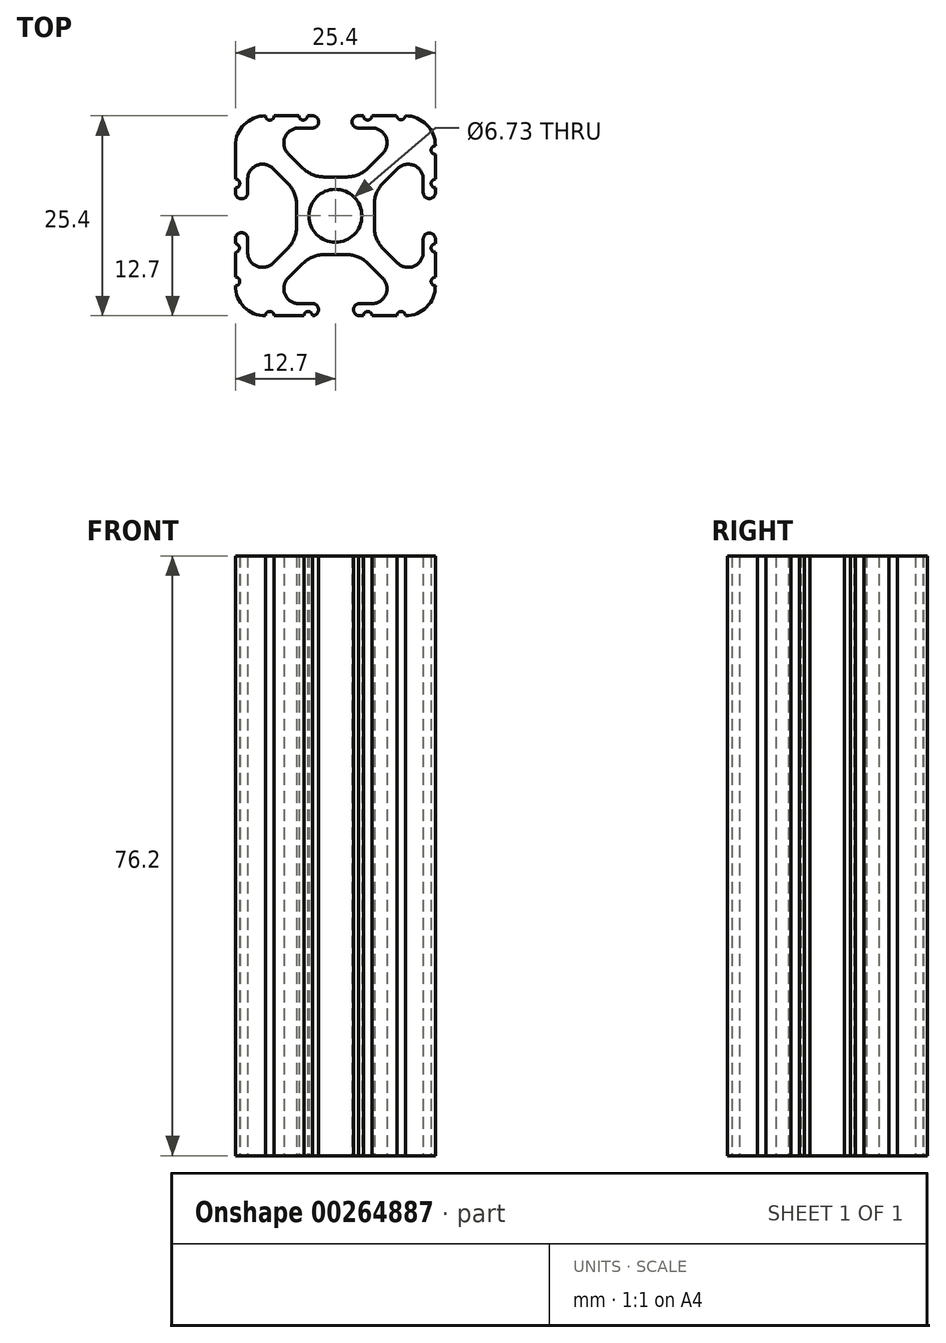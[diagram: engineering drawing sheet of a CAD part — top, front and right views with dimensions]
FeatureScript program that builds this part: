
annotation { "Feature Type Name" : "Feature", "Feature Type Description" : "" }
export const myFeature = defineFeature(function(context is Context, id is Id, definition is map)
    precondition{}
    {
        {
            var Q0;
            Q0=qCreatedBy(makeId("Top.planeOp"),FACE);
            var sketch = newSketch(context, id + "F0", { "sketchPlane" : qUnion([Q0])});
            skCircle(sketch, "E0", {"center": v(-12.7, 12.7) * mm, "radius": 3.36 * mm});
            skLineSegment(sketch, "E1.bottom", {"start": v(-11.24, 17.64) * mm, "end": v(-14.16, 17.64) * mm});
            skLineSegment(sketch, "E1.top", {"start": v(-11.24, 7.76) * mm, "end": v(-14.16, 7.76) * mm});
            skLineSegment(sketch, "E1.left", {"start": v(-7.76, 14.16) * mm, "end": v(-7.76, 11.24) * mm});
            skLineSegment(sketch, "E1.right", {"start": v(-17.64, 14.16) * mm, "end": v(-17.64, 11.24) * mm});
            skPoint(sketch, "E2.visualSharp", {"position": v(-25.4, 25.4) * mm});
            skPoint(sketch, "E3.visualSharp", {"position": v(0, 25.4) * mm});
            skPoint(sketch, "E4.visualSharp", {"position": v(0, 0) * mm});
            skPoint(sketch, "E5.visualSharp", {"position": v(-25.4, 0) * mm});
            skLineSegment(sketch, "E6.0", {"start": v(-18.7, 20.6) * mm, "end": v(-16.85, 18.76) * mm});
            skLineSegment(sketch, "E7.0", {"start": v(-20.6, 18.7) * mm, "end": v(-18.76, 16.85) * mm});
            skPoint(sketch, "E8.orphan", {"position": v(-23.85, 1.55) * mm});
            skPoint(sketch, "E9.orphan", {"position": v(-23.85, 23.85) * mm});
            skPoint(sketch, "E10.orphan", {"position": v(-1.55, 23.85) * mm});
            skPoint(sketch, "E11.orphan", {"position": v(-1.55, 1.55) * mm});
            skLineSegment(sketch, "E12", {"start": v(-8.55, 6.64) * mm, "end": v(-6.7, 4.8) * mm});
            skLineSegment(sketch, "E13.0", {"start": v(-18.7, 4.8) * mm, "end": v(-16.85, 6.64) * mm});
            skLineSegment(sketch, "E14.0", {"start": v(-20.6, 6.7) * mm, "end": v(-18.76, 8.55) * mm});
            skLineSegment(sketch, "E15.0", {"start": v(-8.55, 18.76) * mm, "end": v(-6.7, 20.6) * mm});
            skPoint(sketch, "E16.visualSharp", {"position": v(-23.85, 21.95) * mm});
            skArc(sketch, "E16.filletArc", {"start": v(-20.6, 18.7) * mm, "mid": v(-22.68, 19.1) * mm, "end": v(-23.85, 17.35) * mm});
            skPoint(sketch, "E17.visualSharp", {"position": v(-21.95, 23.85) * mm});
            skArc(sketch, "E17.filletArc", {"start": v(-17.35, 23.85) * mm, "mid": v(-19.1, 22.68) * mm, "end": v(-18.7, 20.6) * mm});
            skPoint(sketch, "E18.visualSharp", {"position": v(-5.34, 23.85) * mm});
            skLineSegment(sketch, "E19", {"start": v(-17.35, 23.85) * mm, "end": v(-15.58, 23.85) * mm});
            skLineSegment(sketch, "E20", {"start": v(-23.85, 17.35) * mm, "end": v(-23.85, 15.62) * mm});
            skLineSegment(sketch, "E21", {"start": v(-8.05, 1.55) * mm, "end": v(-9.78, 1.55) * mm});
            skArc(sketch, "E22.filletArc", {"start": v(-6.7, 20.6) * mm, "mid": v(-6.3, 22.68) * mm, "end": v(-8.05, 23.85) * mm});
            skPoint(sketch, "E23.visualSharp", {"position": v(-1.55, 3.45) * mm});
            skPoint(sketch, "E24.visualSharp", {"position": v(-3.45, 1.55) * mm});
            skArc(sketch, "E24.filletArc", {"start": v(-8.05, 1.55) * mm, "mid": v(-6.3, 2.73) * mm, "end": v(-6.7, 4.8) * mm});
            skArc(sketch, "E25.filletArc", {"start": v(-18.7, 4.8) * mm, "mid": v(-19.1, 2.73) * mm, "end": v(-17.35, 1.55) * mm});
            skArc(sketch, "E26.filletArc", {"start": v(-23.85, 8.05) * mm, "mid": v(-22.68, 6.3) * mm, "end": v(-20.6, 6.7) * mm});
            skLineSegment(sketch, "E27.bottom", {"start": v(-4.9, 0) * mm, "end": v(-8.05, 0) * mm});
            skLineSegment(sketch, "E27.top", {"start": v(-4.92, 25.4) * mm, "end": v(-8.05, 25.4) * mm});
            skLineSegment(sketch, "E27.left", {"start": v(0, 4.9) * mm, "end": v(0, 8.05) * mm});
            skLineSegment(sketch, "E27.right", {"start": v(-25.4, 4.9) * mm, "end": v(-25.4, 8.05) * mm});
            skArc(sketch, "E28.filletArc", {"start": v(-25.4, 3.81) * mm, "mid": v(-24.28, 1.12) * mm, "end": v(-21.59, 0) * mm});
            skArc(sketch, "E29.filletArc", {"start": v(-3.81, 0) * mm, "mid": v(-1.12, 1.12) * mm, "end": v(0, 3.8) * mm});
            skArc(sketch, "E30.filletArc", {"start": v(0, 21.59) * mm, "mid": v(-1.12, 24.28) * mm, "end": v(-3.8, 25.4) * mm});
            skArc(sketch, "E31.filletArc", {"start": v(-21.59, 25.4) * mm, "mid": v(-24.28, 24.28) * mm, "end": v(-25.4, 21.59) * mm});
            skPoint(sketch, "E32.newPointA", {"position": v(-17.64, 7.76) * mm});
            skArc(sketch, "E32.filletArc", {"start": v(-14.16, 7.76) * mm, "mid": v(-15.62, 7.47) * mm, "end": v(-16.85, 6.64) * mm});
            skPoint(sketch, "E33.newPointA", {"position": v(-7.76, 7.76) * mm});
            skArc(sketch, "E33.filletArc", {"start": v(-8.55, 6.64) * mm, "mid": v(-9.78, 7.47) * mm, "end": v(-11.24, 7.76) * mm});
            skArc(sketch, "E34.filletArc", {"start": v(-7.76, 11.24) * mm, "mid": v(-7.47, 9.78) * mm, "end": v(-6.64, 8.55) * mm});
            skArc(sketch, "E35.filletArc", {"start": v(-6.64, 16.85) * mm, "mid": v(-7.47, 15.62) * mm, "end": v(-7.76, 14.16) * mm});
            skPoint(sketch, "E36.newPointB", {"position": v(-7.76, 17.64) * mm});
            skArc(sketch, "E36.filletArc", {"start": v(-11.24, 17.64) * mm, "mid": v(-9.78, 17.93) * mm, "end": v(-8.55, 18.76) * mm});
            skPoint(sketch, "E37.newPointB", {"position": v(-17.64, 17.64) * mm});
            skArc(sketch, "E37.filletArc", {"start": v(-16.85, 18.76) * mm, "mid": v(-15.62, 17.93) * mm, "end": v(-14.16, 17.64) * mm});
            skArc(sketch, "E38.filletArc", {"start": v(-17.64, 14.16) * mm, "mid": v(-17.93, 15.62) * mm, "end": v(-18.76, 16.85) * mm});
            skArc(sketch, "E39.filletArc", {"start": v(-18.76, 8.55) * mm, "mid": v(-17.93, 9.78) * mm, "end": v(-17.64, 11.24) * mm});
            skLineSegment(sketch, "E40", {"start": v(-6.64, 8.55) * mm, "end": v(-4.8, 6.7) * mm});
            skPoint(sketch, "E41.visualSharp", {"position": v(-1.55, 21.95) * mm});
            skArc(sketch, "E42.filletArc", {"start": v(-4.8, 6.7) * mm, "mid": v(-2.73, 6.3) * mm, "end": v(-1.55, 8.05) * mm});
            skLineSegment(sketch, "E43", {"start": v(-1.55, 8.05) * mm, "end": v(-1.55, 9.78) * mm});
            skLineSegment(sketch, "E44", {"start": v(-6.64, 16.85) * mm, "end": v(-4.8, 18.7) * mm});
            skArc(sketch, "E45.filletArc", {"start": v(-1.55, 17.35) * mm, "mid": v(-2.73, 19.1) * mm, "end": v(-4.8, 18.7) * mm});
            skArc(sketch, "E46", {"start": v(-23.85, 9.78) * mm, "mid": v(-24.63, 10.56) * mm, "end": v(-25.4, 9.78) * mm});
            skArc(sketch, "E47", {"start": v(-25.4, 15.62) * mm, "mid": v(-24.63, 14.86) * mm, "end": v(-23.85, 15.62) * mm});
            skArc(sketch, "E48", {"start": v(-15.62, 23.85) * mm, "mid": v(-14.83, 24.63) * mm, "end": v(-15.62, 25.4) * mm});
            skArc(sketch, "E49", {"start": v(-9.78, 25.4) * mm, "mid": v(-10.6, 24.63) * mm, "end": v(-9.78, 23.85) * mm});
            skArc(sketch, "E50", {"start": v(-1.55, 15.62) * mm, "mid": v(-0.77, 14.88) * mm, "end": v(0, 15.62) * mm});
            skArc(sketch, "E51", {"start": v(0, 9.78) * mm, "mid": v(-0.77, 10.5) * mm, "end": v(-1.55, 9.78) * mm});
            skArc(sketch, "E52", {"start": v(-9.78, 1.55) * mm, "mid": v(-10.4, 0.77) * mm, "end": v(-9.78, 0) * mm});
            skArc(sketch, "E53", {"start": v(-15.62, 0) * mm, "mid": v(-14.85, 0.77) * mm, "end": v(-15.62, 1.55) * mm});
            skLineSegment(sketch, "E54.trimOffspring", {"start": v(-15.62, 1.55) * mm, "end": v(-17.35, 1.55) * mm});
            skLineSegment(sketch, "E55.trimOffspring", {"start": v(-16.7, 0) * mm, "end": v(-20.5, 0) * mm});
            skLineSegment(sketch, "E56.trimOffspring", {"start": v(-1.55, 15.62) * mm, "end": v(-1.55, 17.35) * mm});
            skLineSegment(sketch, "E57.trimOffspring", {"start": v(0, 15.62) * mm, "end": v(0, 16.26) * mm});
            skLineSegment(sketch, "E58.trimOffspring", {"start": v(-23.85, 9.78) * mm, "end": v(-23.85, 8.05) * mm});
            skLineSegment(sketch, "E59.trimOffspring", {"start": v(-25.4, 15.62) * mm, "end": v(-25.4, 16.26) * mm});
            skLineSegment(sketch, "E60.trimOffspring", {"start": v(-9.86, 23.85) * mm, "end": v(-8.05, 23.85) * mm});
            skLineSegment(sketch, "E61.trimOffspring", {"start": v(-15.58, 25.4) * mm, "end": v(-16.25, 25.4) * mm});
            skPoint(sketch, "E62.start.orphan", {"position": v(-15.62, 17.93) * mm});
            skPoint(sketch, "E63.start.orphan", {"position": v(-9.78, 17.93) * mm});
            skPoint(sketch, "E64.start.orphan", {"position": v(-7.47, 15.62) * mm});
            skPoint(sketch, "E65.start.orphan", {"position": v(-7.47, 9.78) * mm});
            skPoint(sketch, "E66.start.orphan", {"position": v(-17.93, 15.62) * mm});
            skPoint(sketch, "E67.start.orphan", {"position": v(-17.93, 9.78) * mm});
            skPoint(sketch, "E68.start.orphan", {"position": v(-9.78, 7.47) * mm});
            skPoint(sketch, "E69.start.orphan", {"position": v(-15.62, 7.47) * mm});
            skPoint(sketch, "E70.endSnap0", {"position": v(0, 18.6) * mm});
            skPoint(sketch, "E71.startSnap0", {"position": v(-1.55, 8.92) * mm});
            skArc(sketch, "E72", {"start": v(-4.92, 25.4) * mm, "mid": v(-4.37, 24.9) * mm, "end": v(-3.81, 25.4) * mm});
            skArc(sketch, "E73", {"start": v(-9.14, 25.4) * mm, "mid": v(-8.6, 24.86) * mm, "end": v(-8.05, 25.4) * mm});
            skArc(sketch, "E74", {"start": v(-17.35, 25.4) * mm, "mid": v(-16.8, 24.86) * mm, "end": v(-16.25, 25.4) * mm});
            skArc(sketch, "E75", {"start": v(-21.6, 25.4) * mm, "mid": v(-21.04, 24.85) * mm, "end": v(-20.49, 25.4) * mm});
            skLineSegment(sketch, "E76", {"start": v(-25.4, 21.59) * mm, "end": v(-25.4, 20.5) * mm});
            skArc(sketch, "E77", {"start": v(-25.4, 16.26) * mm, "mid": v(-24.84, 16.8) * mm, "end": v(-25.4, 17.35) * mm});
            skArc(sketch, "E78", {"start": v(-25.4, 8.05) * mm, "mid": v(-24.9, 8.6) * mm, "end": v(-25.4, 9.15) * mm});
            skArc(sketch, "E79", {"start": v(-25.4, 3.81) * mm, "mid": v(-24.85, 4.36) * mm, "end": v(-25.4, 4.9) * mm});
            skArc(sketch, "E80", {"start": v(-20.5, 0) * mm, "mid": v(-21.04, 0.55) * mm, "end": v(-21.59, 0) * mm});
            skArc(sketch, "E81", {"start": v(-15.62, 0) * mm, "mid": v(-16.16, 0.54) * mm, "end": v(-16.7, 0) * mm});
            skArc(sketch, "E82", {"start": v(-8.05, 0) * mm, "mid": v(-8.6, 0.55) * mm, "end": v(-9.15, 0) * mm});
            skArc(sketch, "E83", {"start": v(-3.81, 0) * mm, "mid": v(-4.35, 0.54) * mm, "end": v(-4.9, 0) * mm});
            skLineSegment(sketch, "E84.trimOffspring", {"start": v(-17.35, 25.4) * mm, "end": v(-20.49, 25.4) * mm});
            skLineSegment(sketch, "E85.trimOffspring", {"start": v(-25.4, 17.35) * mm, "end": v(-25.4, 21.59) * mm});
            skLineSegment(sketch, "E86.trimOffspring", {"start": v(-25.4, 9.15) * mm, "end": v(-25.4, 9.78) * mm});
            skLineSegment(sketch, "E87.trimOffspring", {"start": v(-9.15, 0) * mm, "end": v(-9.78, 0) * mm});
            skArc(sketch, "E88", {"start": v(0, 4.9) * mm, "mid": v(-0.54, 4.36) * mm, "end": v(0, 3.8) * mm});
            skArc(sketch, "E89", {"start": v(0, 9.15) * mm, "mid": v(-0.54, 8.6) * mm, "end": v(0, 8.05) * mm});
            skLineSegment(sketch, "E90.trimOffspring", {"start": v(0, 9.15) * mm, "end": v(0, 9.78) * mm});
            skArc(sketch, "E91", {"start": v(0, 21.59) * mm, "mid": v(-0.55, 21.04) * mm, "end": v(0, 20.5) * mm});
            skArc(sketch, "E92", {"start": v(0, 17.35) * mm, "mid": v(-0.55, 16.8) * mm, "end": v(0, 16.26) * mm});
            skLineSegment(sketch, "E93.trimOffspring", {"start": v(0, 17.35) * mm, "end": v(0, 20.5) * mm});
            skLineSegment(sketch, "E94.trimOffspring", {"start": v(-9.14, 25.4) * mm, "end": v(-9.86, 25.4) * mm});
            skSolve(sketch);
        }
        {
            var Q0;
            Q0=qSketchRegion(id+"F0",true);
            extrude(context, id + "F1", {"entities" : qUnion([Q0]), "depth" : 76.2 * mm});
        }
    });
